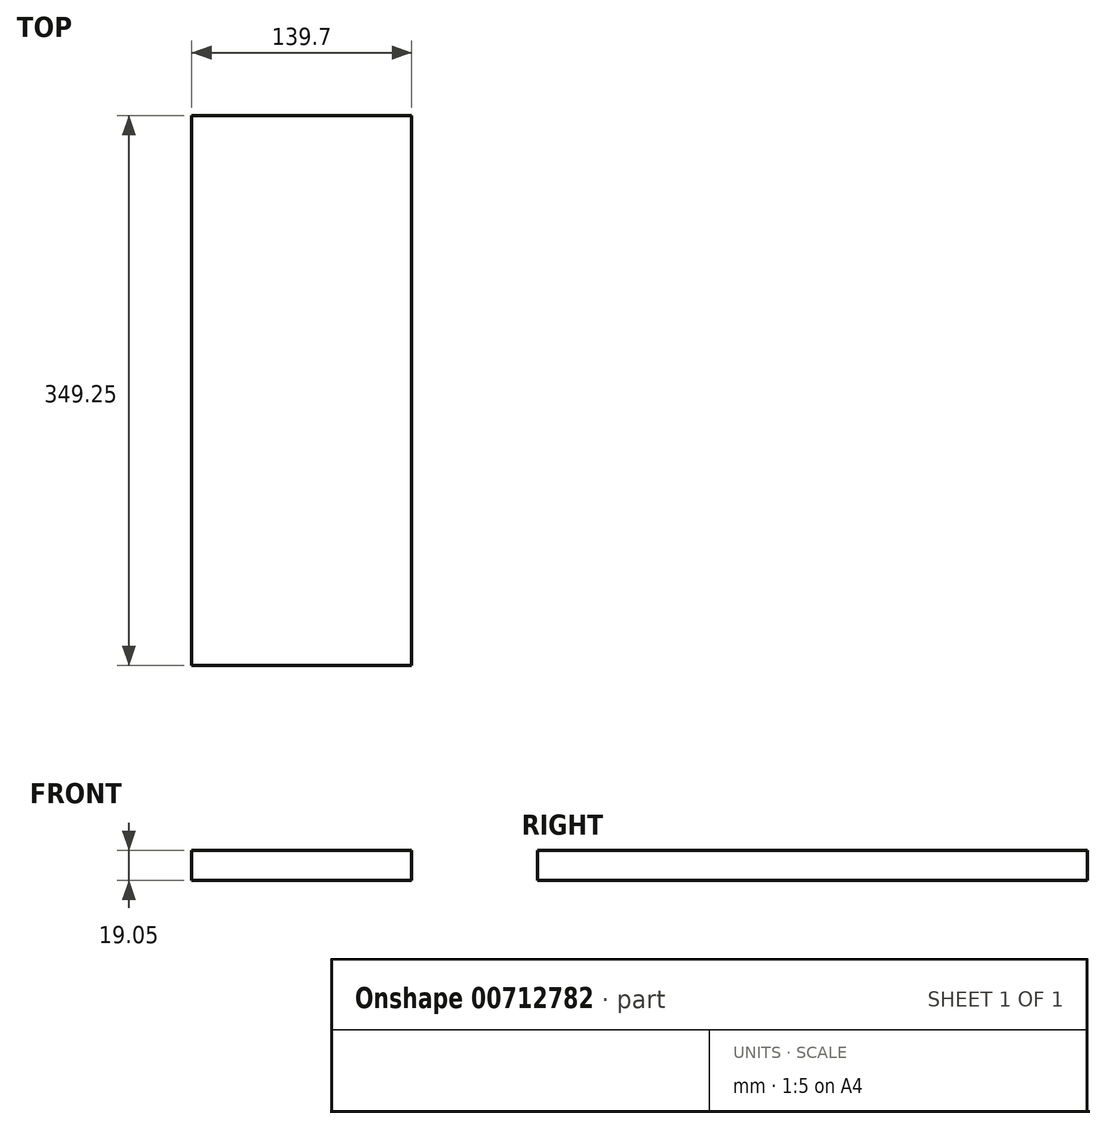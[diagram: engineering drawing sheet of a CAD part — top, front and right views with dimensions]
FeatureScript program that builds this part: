
annotation { "Feature Type Name" : "Feature", "Feature Type Description" : "" }
export const myFeature = defineFeature(function(context is Context, id is Id, definition is map)
    precondition{}
    {
        {
            var Q0;
            Q0=qCreatedBy(makeId("Front.planeOp"),FACE);
            var sketch = newSketch(context, id + "F0", { "sketchPlane" : qUnion([Q0])});
            skLineSegment(sketch, "E0.bottom", {"start": v(0, 0) * mm, "end": v(-139.7, 0) * mm});
            skLineSegment(sketch, "E0.top", {"start": v(0, 19.05) * mm, "end": v(-139.7, 19.05) * mm});
            skLineSegment(sketch, "E0.left", {"start": v(0, 0) * mm, "end": v(0, 19.05) * mm});
            skLineSegment(sketch, "E0.right", {"start": v(-139.7, 0) * mm, "end": v(-139.7, 19.05) * mm});
            skSolve(sketch);
        }
        {
            var Q0;
            Q0 = qSketchRegion(id + "F0", true);
            extrude(context, id + "F1", {"entities" : qUnion([Q0]), "depth" : 349.25 * mm, "offsetDistance" : 25.4 * mm});
        }
    });
